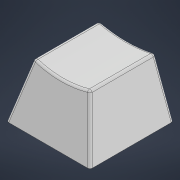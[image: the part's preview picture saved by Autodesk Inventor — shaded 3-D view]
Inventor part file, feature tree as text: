
AUTODESK INVENTOR PART (.ipt)
format: ipt  version: 2022 (Build 260153000, 153)  size: 232,960 bytes
history: native  units: mm
features: sketch x4, other x4, extrude x4, fillet x3, shell x1
ambient origin geometry x8: Origin, YZ Plane, XZ Plane, XY Plane, X Axis, Y Axis, Z Axis, Center Point
bodies: Body1 (feature_tree)
feature tree (16):
  sketch  "スケッチ1"
  other  "作業平面7"
  other  "作業平面9"
  other  "作業平面10"
  other  "作業平面11"
  sketch  "スケッチ10"
  sketch  "スケッチ11"
  extrude  "押し出し2"  Depth=18.0mm
  extrude  "押し出し3"  Depth=18.0mm
  extrude  "押し出し4"  Depth=11.76mm
  shell  "シェル1"  Thickness=12.0mm
  fillet  "フィレット1"  Radius=18.0mm
  fillet  "フィレット2"  Radius=11.0mm
  fillet  "フィレット3"  Radius=14.0mm
  extrude  "押し出し5"  Depth=18.0mm
  sketch  "スケッチ12"
